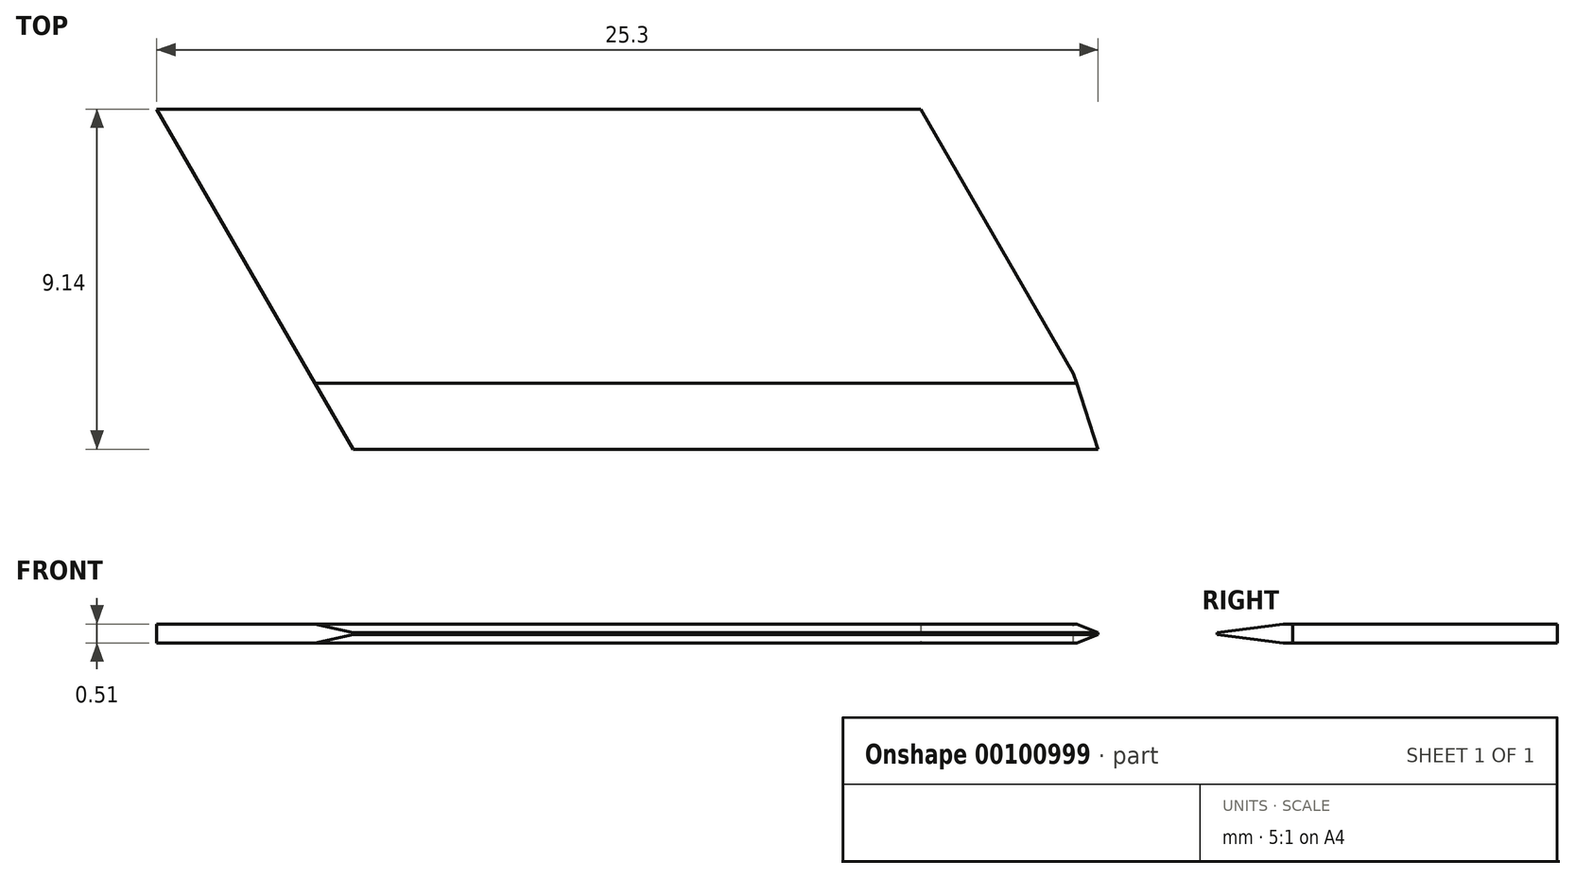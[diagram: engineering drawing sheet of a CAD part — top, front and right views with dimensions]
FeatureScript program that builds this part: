
annotation { "Feature Type Name" : "Feature", "Feature Type Description" : "" }
export const myFeature = defineFeature(function(context is Context, id is Id, definition is map)
    precondition{}
    {
        {
            var Q0;
            Q0=qCreatedBy(makeId("Top.planeOp"),FACE);
            var sketch = newSketch(context, id + "F0", { "sketchPlane" : qUnion([Q0])});
            skLineSegment(sketch, "E0", {"start": v(0, 0) * mm, "end": v(20.53, 0) * mm});
            skLineSegment(sketch, "E1", {"start": v(20.53, 0) * mm, "end": v(25.8, -9.14) * mm});
            skLineSegment(sketch, "E2", {"start": v(25.8, -9.14) * mm, "end": v(5.28, -9.14) * mm});
            skLineSegment(sketch, "E3", {"start": v(5.28, -9.14) * mm, "end": v(0, 0) * mm});
            skSolve(sketch);
        }
        {
            var Q0;
            Q0 = qSketchRegion(id + "F0", true);
            extrude(context, id + "F1", {"entities" : qUnion([Q0]), "depth" : 0.5 * mm});
        }
        {
            var Q0;
            Q0=makeQuery(id+"F1.opExtrude","CAP_FACE",FACE,{"disambiguationData":[OSD([sQuery(id+"F0.wireOp",EDGE,"E0"),sQuery(id+"F0.wireOp",EDGE,"E1"),sQuery(id+"F0.wireOp",EDGE,"E2"),sQuery(id+"F0.wireOp",EDGE,"E3")])],"isStart":false});
            var sketch = newSketch(context, id + "F2", { "sketchPlane" : qUnion([Q0])});
            skLineSegment(sketch, "E4", {"start": v(25.8, -9.14) * mm, "end": v(24.64, -7.11) * mm});
            skLineSegment(sketch, "E5", {"start": v(24.64, -7.11) * mm, "end": v(25.3, -9.14) * mm});
            skLineSegment(sketch, "E6", {"start": v(25.3, -9.14) * mm, "end": v(25.8, -9.14) * mm});
            skSolve(sketch);
        }
        {
            var Q0;
            Q0=makeQuery(id+"F1.opExtrude","CAP_EDGE",EDGE,{"disambiguationData":[OSD([sQuery(id+"F0.wireOp",EDGE,"E2")])],"isStart":false});
            var Q1;
            Q1=makeQuery(id+"F1.opExtrude","CAP_EDGE",EDGE,{"disambiguationData":[OSD([sQuery(id+"F0.wireOp",EDGE,"E2")])],"isStart":true});
            chamfer(context, id + "F3", {"entities" : qUnion([Q0, Q1]), "chamferType" : ChamferType.TWO_OFFSETS, "width1" : 0.23 * mm, "oppositeDirection" : false, "width2" : 1.78 * mm, "tangentPropagation" : true});
        }
        {
            var Q0;
            Q0 = qSketchRegion(id + "F2", true);
            extrude(context, id + "F4", {"entities" : qUnion([Q0]), "operationType" : NewBodyOperationType.REMOVE, "oppositeDirection" : true, "depth" : 25.4 * mm});
        }
    });
